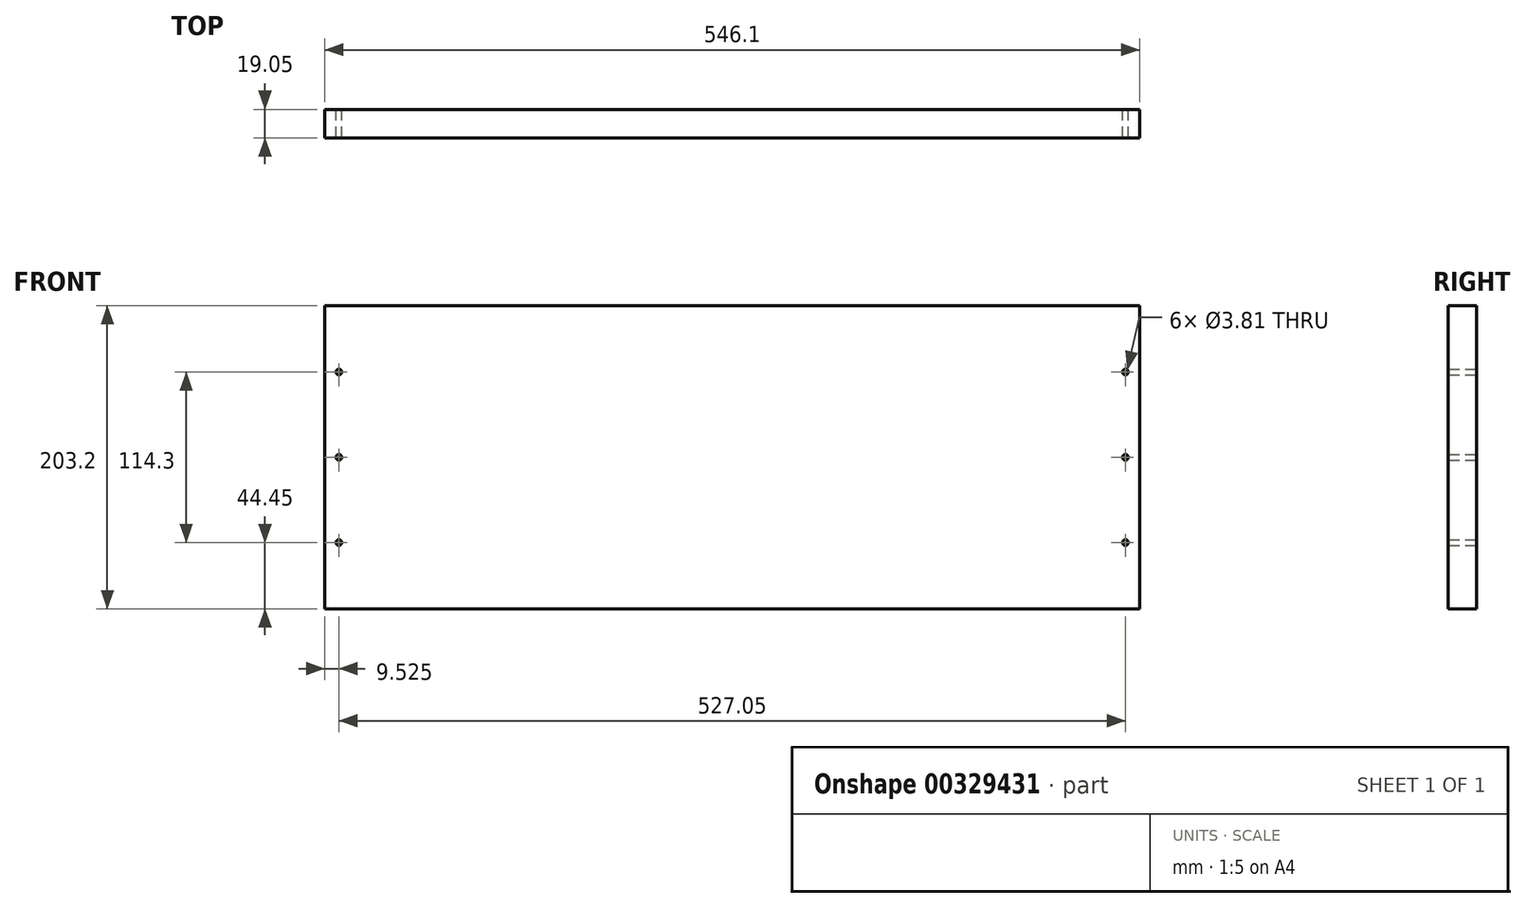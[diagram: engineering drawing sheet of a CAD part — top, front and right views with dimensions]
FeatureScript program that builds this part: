
annotation { "Feature Type Name" : "Feature", "Feature Type Description" : "" }
export const myFeature = defineFeature(function(context is Context, id is Id, definition is map)
    precondition{}
    {
        {
            var Q0;
            Q0=qCreatedBy(makeId("Front.planeOp"),FACE);
            var sketch = newSketch(context, id + "F0", { "sketchPlane" : qUnion([Q0])});
            skLineSegment(sketch, "E0.bottom", {"start": v(-273.05, -101.6) * mm, "end": v(273.05, -101.6) * mm});
            skLineSegment(sketch, "E0.top", {"start": v(-273.05, 101.6) * mm, "end": v(273.05, 101.6) * mm});
            skLineSegment(sketch, "E0.left", {"start": v(-273.05, -101.6) * mm, "end": v(-273.05, 101.6) * mm});
            skLineSegment(sketch, "E0.right", {"start": v(273.05, -101.6) * mm, "end": v(273.05, 101.6) * mm});
            skPoint(sketch, "E0.middle", {"position": v(0, 0) * mm});
            skSolve(sketch);
        }
        {
            var Q0;
            Q0 = qSketchRegion(id + "F0", true);
            extrude(context, id + "F1", {"entities" : qUnion([Q0]), "depth" : 19.05 * mm});
        }
        {
            var Q0;
            Q0=makeQuery(id+"F1.opExtrude","CAP_FACE",FACE,{"disambiguationData":[OSD([sQuery(id+"F0.wireOp",EDGE,"E0.bottom"),sQuery(id+"F0.wireOp",EDGE,"E0.top"),sQuery(id+"F0.wireOp",EDGE,"E0.left"),sQuery(id+"F0.wireOp",EDGE,"E0.right")])],"isStart":true});
            var sketch = newSketch(context, id + "F2", { "sketchPlane" : qUnion([Q0])});
            skCircle(sketch, "E1", {"center": v(-263.52, 57.15) * mm, "radius": 1.9 * mm});
            skLineSegment(sketch, "E2", {"start": v(-263.52, 101.6) * mm, "end": v(-263.52, -101.6) * mm, "construction": true});
            skCircle(sketch, "E3", {"center": v(-263.52, 0) * mm, "radius": 1.9 * mm});
            skCircle(sketch, "E4", {"center": v(-263.52, -57.15) * mm, "radius": 1.9 * mm});
            skCircle(sketch, "E5.MirrorC", {"center": v(263.52, 57.15) * mm, "radius": 1.9 * mm});
            skCircle(sketch, "E6.MirrorC", {"center": v(263.52, -57.15) * mm, "radius": 1.9 * mm});
            skCircle(sketch, "E7.MirrorC", {"center": v(263.52, 0) * mm, "radius": 1.9 * mm});
            skLineSegment(sketch, "E8.MirrorCS", {"start": v(263.52, 101.6) * mm, "end": v(263.52, -101.6) * mm, "construction": true});
            skSolve(sketch);
        }
        {
            var Q0;
            Q0 = qSketchRegion(id + "F2", true);
            extrude(context, id + "F3", {"entities" : qUnion([Q0]), "operationType" : NewBodyOperationType.REMOVE, "endBound" : BoundingType.THROUGH_ALL, "oppositeDirection" : true, "depth" : 19.05 * mm});
        }
    });
